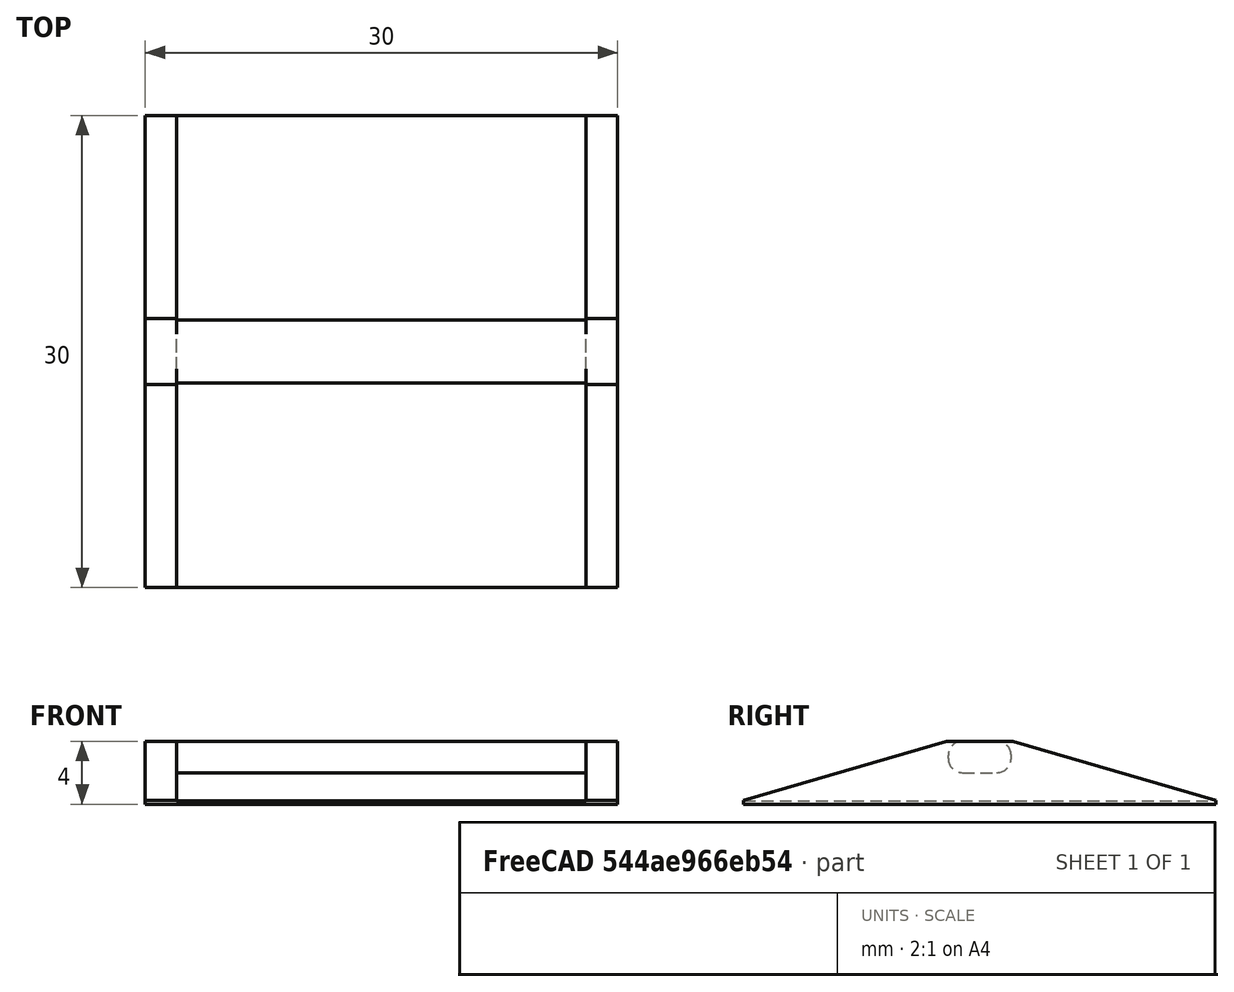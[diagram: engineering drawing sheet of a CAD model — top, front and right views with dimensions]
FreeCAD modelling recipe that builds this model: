
FCSTD DOCUMENT  (FreeCAD 0.18RUnknown)
Label: StrapHolder
License: All rights reserved
LicenseURL: http://en.wikipedia.org/wiki/All_rights_reserved
objects: Part::Box×4, Part::Fillet×1, Part::MultiFuse×1, Part::Chamfer×1
note: 7 computed .brp shape members not serialized (recipe doc carries the construction recipe); baked Part::Feature solids carry a one-line shape summary decoded from their .brp

FEATURE [Part::Box] Box  label="base"
  AttacherType = Attacher::AttachEngine3D
  Height = 0.2
  Length = 30
  Width = 30
FEATURE [Part::Box] Box001  label="Куб001"
  AttacherType = Attacher::AttachEngine3D
  Height = 4
  Length = 2
  Width = 30
FEATURE [Part::Box] Box002  label="Куб002"
  AttacherType = Attacher::AttachEngine3D
  Height = 4
  Length = 2
  Placement = pos=(28,0,0) rot=(0,0,1;0rad)
  Width = 30
FEATURE [Part::Box] Box003  label="CentralBar"
  AttacherType = Attacher::AttachEngine3D
  Height = 2
  Length = 26
  Placement = pos=(2,13,2) rot=(0,0,1;0rad)
  Width = 4
FEATURE [Part::Fillet] Fillet
  Base = -> Box003
  Edges = 4 edges r=0.9: [Edge9,Edge10,Edge11,Edge12]
FEATURE [Part::MultiFuse] Fusion
  Shapes = -> [Box,Box001,Box002,Fillet]
FEATURE [Part::Chamfer] Chamfer  label="StrapAssembly"
  Base = -> Fusion
  Edges = 4 edges: [Edge19 r1=3.75 r2=12.9,Edge20 r1=12.9 r2=3.75,Edge50 r1=3.75 r2=12.9,Edge68 r1=12.9 r2=3.75]
